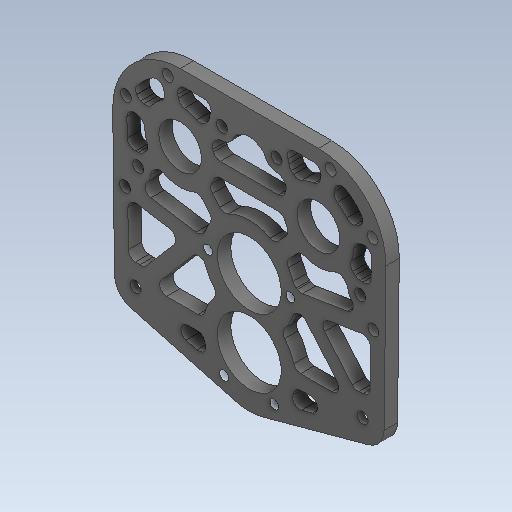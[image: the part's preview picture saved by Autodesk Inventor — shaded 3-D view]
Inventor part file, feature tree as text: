
AUTODESK INVENTOR PART (.ipt)
format: ipt  version: 2020 (Build 240168000, 168)  size: 384,512 bytes
history: native  units: in
note: dims shown in document units (in); Inventor stores cm internally (conversion verified against a paired STEP export)
features: fillet x1
ambient origin geometry x8: Origin, YZ Plane, XZ Plane, XY Plane, X Axis, Y Axis, Z Axis, Center Point
bodies: Solid1 (feature_tree)
feature tree (1):
  fillet  "Fillet2"  [1 undecoded]
note: 1 required parameter value undecoded (feature->parameter linkage not recoverable at this tier; creation-order binding heuristic only, values carry confidence <= 0.55)
